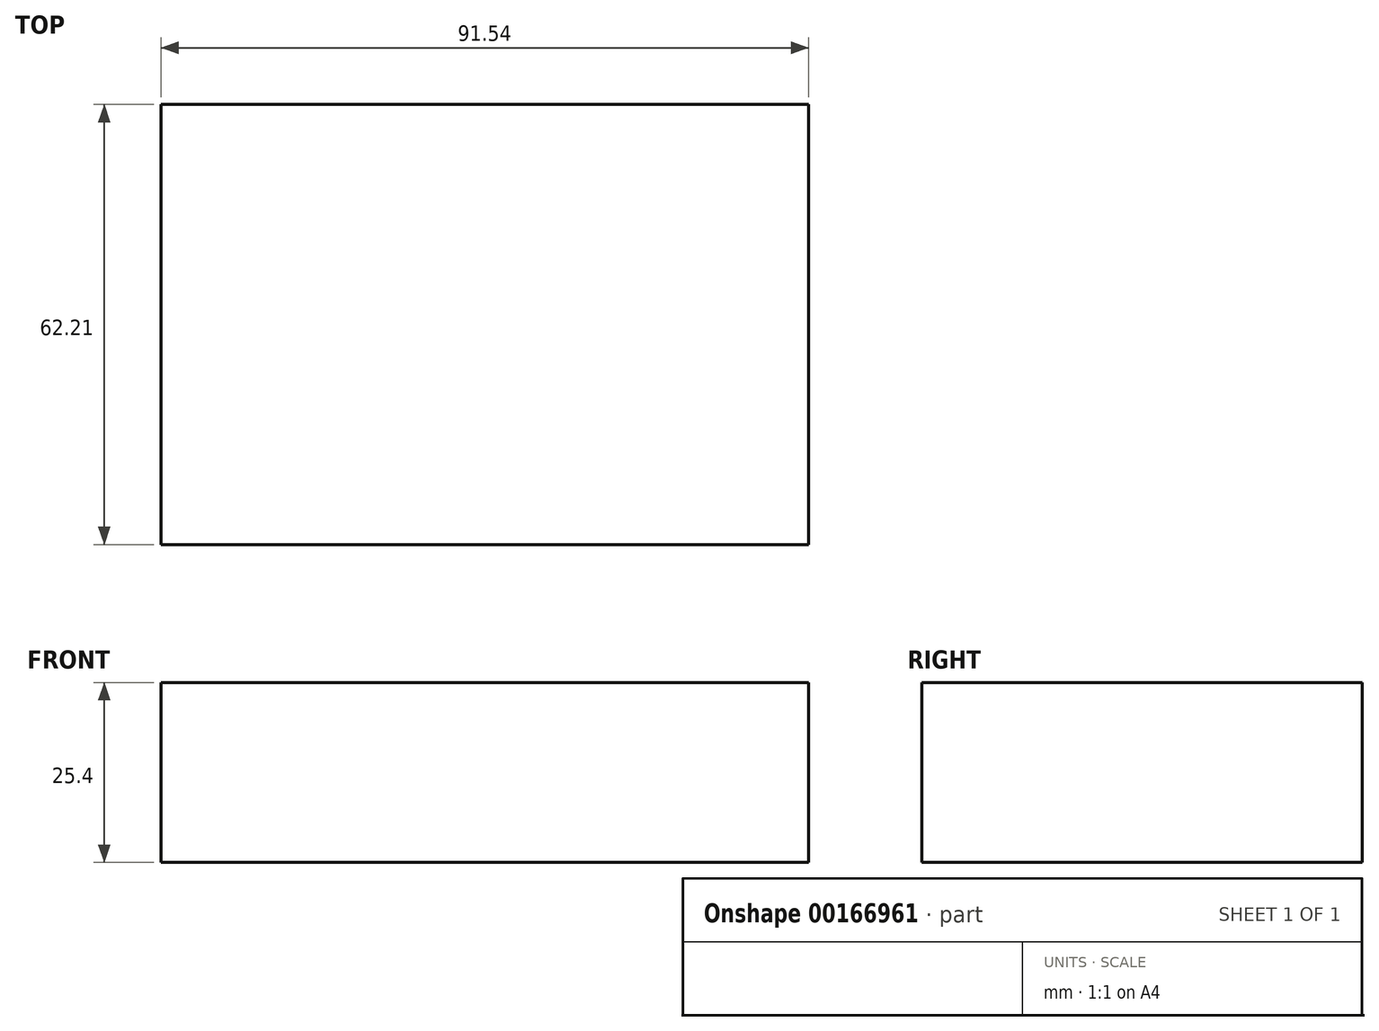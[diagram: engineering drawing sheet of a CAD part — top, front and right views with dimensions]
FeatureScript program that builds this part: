
annotation { "Feature Type Name" : "Feature", "Feature Type Description" : "" }
export const myFeature = defineFeature(function(context is Context, id is Id, definition is map)
    precondition{}
    {
        {
            var Q0;
            Q0=qCreatedBy(makeId("Top.planeOp"),FACE);
            var sketch = newSketch(context, id + "F0", { "sketchPlane" : qUnion([Q0])});
            skLineSegment(sketch, "E0.bottom", {"start": v(0, 0) * mm, "end": v(91.54, 0) * mm});
            skLineSegment(sketch, "E0.top", {"start": v(0, -62.2) * mm, "end": v(91.54, -62.2) * mm});
            skLineSegment(sketch, "E0.left", {"start": v(0, 0) * mm, "end": v(0, -62.2) * mm});
            skLineSegment(sketch, "E0.right", {"start": v(91.54, 0) * mm, "end": v(91.54, -62.2) * mm});
            skSolve(sketch);
        }
        {
            var Q0;
            Q0 = qSketchRegion(id + "F0", true);
            extrude(context, id + "F1", {"entities" : qUnion([Q0]), "depth" : 25.4 * mm});
        }
    });
